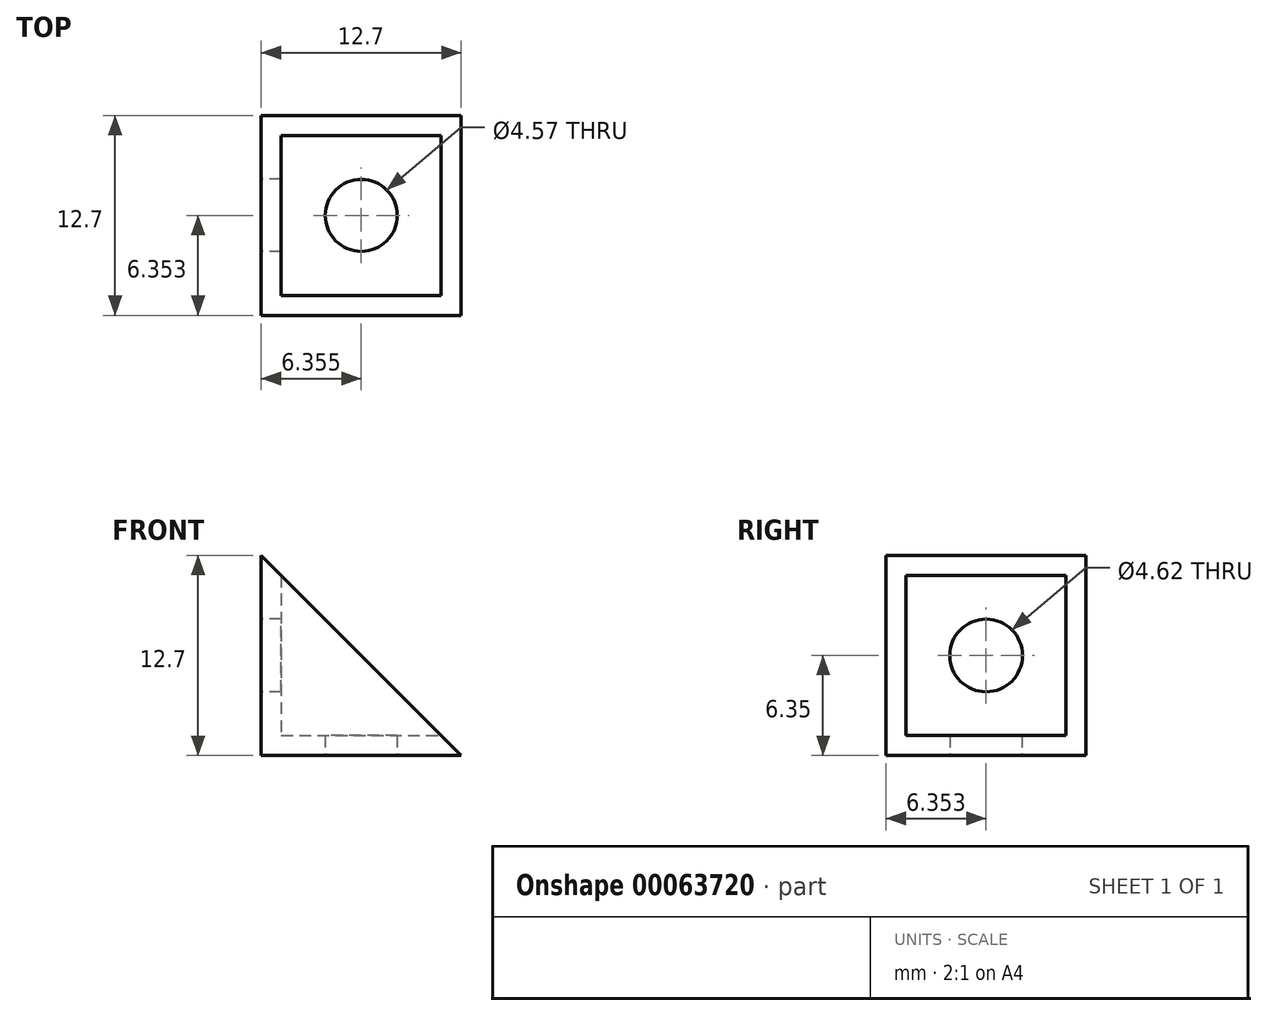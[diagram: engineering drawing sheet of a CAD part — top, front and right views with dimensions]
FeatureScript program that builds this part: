
annotation { "Feature Type Name" : "Feature", "Feature Type Description" : "" }
export const myFeature = defineFeature(function(context is Context, id is Id, definition is map)
    precondition{}
    {
        {
            var Q0;
            Q0=qCreatedBy(makeId("Top.planeOp"),FACE);
            var sketch = newSketch(context, id + "F0", { "sketchPlane" : qUnion([Q0])});
            skLineSegment(sketch, "E0.bottom", {"start": v(-2.03, 9.46) * mm, "end": v(10.67, 9.46) * mm});
            skLineSegment(sketch, "E0.top", {"start": v(-2.03, -3.24) * mm, "end": v(10.67, -3.24) * mm});
            skLineSegment(sketch, "E0.left", {"start": v(-2.03, 9.46) * mm, "end": v(-2.03, -3.24) * mm});
            skLineSegment(sketch, "E0.right", {"start": v(10.67, 9.46) * mm, "end": v(10.67, -3.24) * mm});
            skSolve(sketch);
        }
        {
            var Q0;
            Q0=makeQuery(id+"F0.imprint","IMPRINT",FACE,{"disambiguationData":[TD([[makeQuery(id+"F0.imprint","IMPRINT",EDGE,{"derivedFrom":sQuery(id+"F0.wireOp",EDGE,"E0.bottom")}),-1.0]])]});
            extrude(context, id + "F1", {"entities" : qUnion([Q0]), "depth" : 12.7 * mm});
        }
        {
            var Q0;
            Q0=makeQuery(id+"F1.opExtrude","SWEPT_FACE",FACE,{"disambiguationData":[OSD([sQuery(id+"F0.wireOp",EDGE,"E0.top")])]});
            var sketch = newSketch(context, id + "F2", { "sketchPlane" : qUnion([Q0])});
            skLineSegment(sketch, "E1", {"start": v(-2.03, 12.7) * mm, "end": v(10.67, 0) * mm});
            skSolve(sketch);
        }
        {
            var Q0;
            Q0=makeQuery(id+"F2.imprint","IMPRINT",FACE,{"disambiguationData":[TD([[makeQuery(id+"F2.imprint","IMPRINT",EDGE,{"derivedFrom":sQuery(id+"F2.wireOp",EDGE,"E1")}),1.0]])]});
            extrude(context, id + "F3", {"entities" : qUnion([Q0]), "operationType" : NewBodyOperationType.REMOVE, "oppositeDirection" : true, "depth" : 25.4 * mm});
        }
        {
            var Q0;
            Q0=makeQuery(id+"F3.boolean.opBoolean","COPY",FACE,{"derivedFrom":makeQuery(id+"F3.opExtrude","SWEPT_FACE",FACE,{"disambiguationData":[OSD([sQuery(id+"F2.wireOp",EDGE,"E1")])]})});
            shell(context, id + "F4", {"entities" : qUnion([Q0]), "thickness" : 1.27 * mm});
        }
        {
            var Q0;
            Q0=makeQuery(id+"F1.opExtrude","CAP_FACE",FACE,{"disambiguationData":[OSD([sQuery(id+"F0.wireOp",EDGE,"E0.bottom"),sQuery(id+"F0.wireOp",EDGE,"E0.top"),sQuery(id+"F0.wireOp",EDGE,"E0.left"),sQuery(id+"F0.wireOp",EDGE,"E0.right")])],"isStart":true});
            var sketch = newSketch(context, id + "F5", { "sketchPlane" : qUnion([Q0])});
            skLineSegment(sketch, "E2", {"start": v(4.32, 3.24) * mm, "end": v(4.32, -9.46) * mm});
            skCircle(sketch, "E3", {"center": v(4.32, -3.11) * mm, "radius": 2.29 * mm});
            skSolve(sketch);
        }
        {
            var Q0;
            Q0=makeQuery(id+"F1.opExtrude","SWEPT_FACE",FACE,{"disambiguationData":[OSD([sQuery(id+"F0.wireOp",EDGE,"E0.left")])]});
            var sketch = newSketch(context, id + "F6", { "sketchPlane" : qUnion([Q0])});
            skLineSegment(sketch, "E4", {"start": v(-3.11, 12.7) * mm, "end": v(-3.11, 0) * mm});
            skCircle(sketch, "E5", {"center": v(-3.11, 6.35) * mm, "radius": 2.31 * mm});
            skSolve(sketch);
        }
        {
            var Q0;
            {var subQ0=sQuery(id+"F6.wireOp",EDGE,"E5");var subQ1=sQuery(id+"F6.wireOp",EDGE,"E4");var subQ2=makeQuery(id+"F6.imprint","INTERSECT",VERTEX,{"disambiguationData":[OD(0.0)],"derivedFrom":[subQ1,subQ0]});Q0=makeQuery(id+"F6.imprint","IMPRINT",FACE,{"disambiguationData":[TD([[makeQuery(id+"F6.imprint","IMPRINT",EDGE,{"disambiguationData":[TD([[subQ2,-1.0]])],"derivedFrom":subQ1}),1.0]])]});}
            var Q1;
            {var subQ0=sQuery(id+"F6.wireOp",EDGE,"E5");var subQ1=sQuery(id+"F6.wireOp",EDGE,"E4");var subQ2=makeQuery(id+"F6.imprint","INTERSECT",VERTEX,{"disambiguationData":[OD(0.0)],"derivedFrom":[subQ1,subQ0]});Q1=makeQuery(id+"F6.imprint","IMPRINT",FACE,{"disambiguationData":[TD([[makeQuery(id+"F6.imprint","IMPRINT",EDGE,{"disambiguationData":[TD([[subQ2,-1.0]])],"derivedFrom":subQ1}),-1.0]])]});}
            extrude(context, id + "F7", {"entities" : qUnion([Q0, Q1]), "operationType" : NewBodyOperationType.REMOVE, "oppositeDirection" : true, "depth" : 25.4 * mm});
        }
        {
            var Q0;
            {var subQ0=sQuery(id+"F5.wireOp",EDGE,"E3");var subQ1=sQuery(id+"F5.wireOp",EDGE,"E2");var subQ2=makeQuery(id+"F5.imprint","INTERSECT",VERTEX,{"disambiguationData":[OD(0.0)],"derivedFrom":[subQ1,subQ0]});Q0=makeQuery(id+"F5.imprint","IMPRINT",FACE,{"disambiguationData":[TD([[makeQuery(id+"F5.imprint","IMPRINT",EDGE,{"disambiguationData":[TD([[subQ2,-1.0]])],"derivedFrom":subQ1}),1.0]])]});}
            var Q1;
            {var subQ0=sQuery(id+"F5.wireOp",EDGE,"E3");var subQ1=sQuery(id+"F5.wireOp",EDGE,"E2");var subQ2=makeQuery(id+"F5.imprint","INTERSECT",VERTEX,{"disambiguationData":[OD(0.0)],"derivedFrom":[subQ1,subQ0]});Q1=makeQuery(id+"F5.imprint","IMPRINT",FACE,{"disambiguationData":[TD([[makeQuery(id+"F5.imprint","IMPRINT",EDGE,{"disambiguationData":[TD([[subQ2,-1.0]])],"derivedFrom":subQ1}),-1.0]])]});}
            extrude(context, id + "F8", {"entities" : qUnion([Q0, Q1]), "operationType" : NewBodyOperationType.REMOVE, "oppositeDirection" : true, "depth" : 25.4 * mm});
        }
    });
